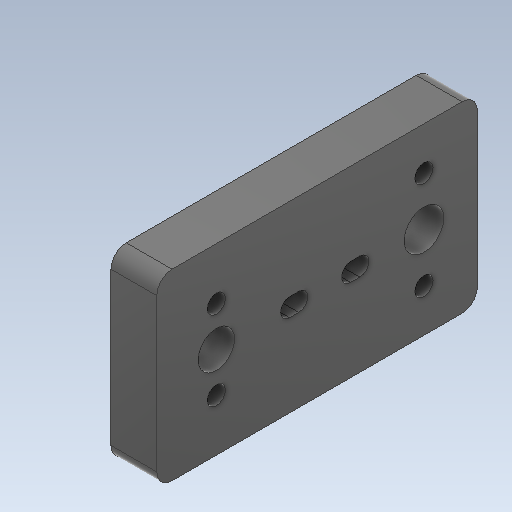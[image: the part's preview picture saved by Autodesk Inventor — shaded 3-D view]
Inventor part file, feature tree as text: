
AUTODESK INVENTOR PART (.ipt)
format: ipt  version: 2020 (Build 240168000, 168)  size: 230,912 bytes
history: native  units: mm
features: extrude x7, sketch x7, chamfer x1, fillet x1
ambient origin geometry x8: Origin, YZ Plane, XZ Plane, XY Plane, X Axis, Y Axis, Z Axis, Center Point
bodies: Solid1 (feature_tree)
feature tree (16):
  extrude  "Extrusion1"  Depth=40.0mm
  extrude  "Extrusion2"  Depth=40.0mm TaperAngle=0.0deg
  extrude  "Extrusion3"  Depth=3.0mm
  extrude  "Extrusion4"  Depth=30.0mm
  extrude  "Extrusion5"  Depth=3.0mm
  extrude  "Extrusion6"  Depth=10.0mm
  extrude  "Extrusion7"  TaperAngle=0.0deg  [1 undecoded]
  chamfer  "Chamfer2"  Distance=30.0mm
  fillet  "Fillet2"  Radius=32.0mm
  sketch  "Sketch1"  dims[d0=15.0mm d1=40.0mm]
  sketch  "Sketch2"  dims[d2=60.0mm d3=40.0mm d4=0.0mm]
  sketch  "Sketch3"  dims[d5=6.0mm d6=3.0mm]
  sketch  "Sketch5"  dims[d7=10.0mm d8=30.0mm]
  sketch  "Sketch6"  dims[d9=0.0mm d10=0.0mm d11=3.0mm]
  sketch  "Sketch7"  dims[d12=6.0mm d13=10.0mm]
  sketch  "Sketch8"  dims[d14=10.0mm d15=0.0mm d16=0.0mm d21=30.0mm d22=0.0mm d23=32.0mm d24=14.0mm d25=17.5mm d26=6.0mm d27=0.0mm d28=0.0mm d29=35.0mm d30=0.0mm d31=13.0mm d32=16.0mm d33=12.0mm d34=6.0mm d35=17.0mm d36=19.5mm d37=26.0mm d38=13.0mm d39=0.0mm d40=0.0mm d41=5.0mm d42=2.0mm d43=45.0deg d44=5.0mm]
note: 1 required parameter value undecoded (feature->parameter linkage not recoverable at this tier; creation-order binding heuristic only, values carry confidence <= 0.55)
